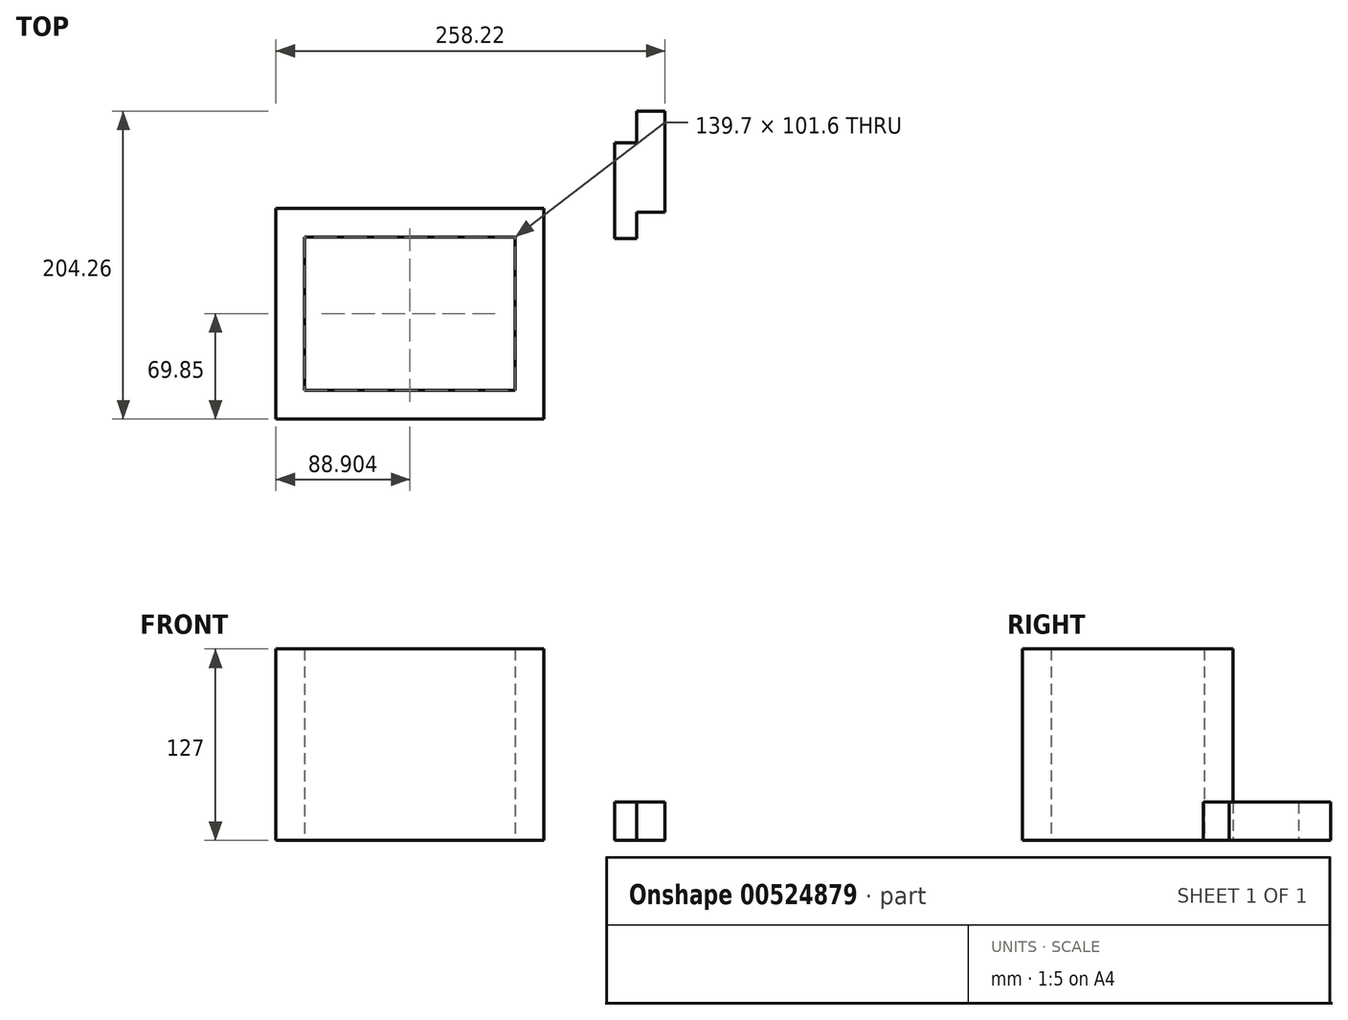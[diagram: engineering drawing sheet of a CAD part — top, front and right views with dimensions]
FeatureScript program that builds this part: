
annotation { "Feature Type Name" : "Feature", "Feature Type Description" : "" }
export const myFeature = defineFeature(function(context is Context, id is Id, definition is map)
    precondition{}
    {
        {
            var Q0;
            Q0=qCreatedBy(makeId("Top.planeOp"),FACE);
            var sketch = newSketch(context, id + "F0", { "sketchPlane" : qUnion([Q0])});
            skLineSegment(sketch, "E0.bottom", {"start": v(-316.12, 0) * mm, "end": v(-297.07, 0) * mm});
            skLineSegment(sketch, "E0.top", {"start": v(-316.12, -139.7) * mm, "end": v(-296.98, -139.7) * mm});
            skLineSegment(sketch, "E0.left", {"start": v(-316.12, 0) * mm, "end": v(-316.12, -139.7) * mm});
            skLineSegment(sketch, "E0.right", {"start": v(-138.32, 0) * mm, "end": v(-138.32, -139.7) * mm});
            skLineSegment(sketch, "E1", {"start": v(-157.37, 0) * mm, "end": v(-157.37, -139.7) * mm});
            skLineSegment(sketch, "E2", {"start": v(-297.07, 0) * mm, "end": v(-297.07, -139.7) * mm});
            skLineSegment(sketch, "E3", {"start": v(-297.07, -19.05) * mm, "end": v(-157.37, -19.05) * mm});
            skLineSegment(sketch, "E4", {"start": v(-297.07, -120.65) * mm, "end": v(-157.37, -120.65) * mm});
            skLineSegment(sketch, "E5", {"start": v(-297.07, 0) * mm, "end": v(-157.37, 0) * mm});
            skLineSegment(sketch, "E6", {"start": v(-157.37, 0) * mm, "end": v(-138.32, 0) * mm});
            skLineSegment(sketch, "E7", {"start": v(-157.37, -139.7) * mm, "end": v(-157.37, -139.7) * mm});
            skLineSegment(sketch, "E8", {"start": v(-296.98, -139.7) * mm, "end": v(-138.32, -139.7) * mm});
            skSolve(sketch);
        }
        {
            var Q0;
            Q0 = qSketchRegion(id + "F0", true);
            extrude(context, id + "F1", {"entities" : qUnion([Q0]), "depth" : 127 * mm, "offsetDistance" : 25.4 * mm});
        }
        {
            var Q0;
            Q0=qCreatedBy(makeId("Top.planeOp"),FACE);
            var sketch = newSketch(context, id + "F2", { "sketchPlane" : qUnion([Q0])});
            skLineSegment(sketch, "E9.bottom", {"start": v(-91.38, 43.53) * mm, "end": v(-76.79, 43.53) * mm});
            skLineSegment(sketch, "E9.top", {"start": v(-91.38, -19.88) * mm, "end": v(-76.79, -19.88) * mm});
            skLineSegment(sketch, "E9.left", {"start": v(-91.38, 43.53) * mm, "end": v(-91.38, -19.88) * mm});
            skLineSegment(sketch, "E9.right", {"start": v(-76.79, 43.53) * mm, "end": v(-76.79, -19.88) * mm});
            skLineSegment(sketch, "E10.bottom", {"start": v(-57.9, -2.56) * mm, "end": v(-76.79, -2.56) * mm});
            skLineSegment(sketch, "E10.top", {"start": v(-57.9, 64.56) * mm, "end": v(-76.79, 64.56) * mm});
            skLineSegment(sketch, "E10.left", {"start": v(-57.9, -2.56) * mm, "end": v(-57.9, 64.56) * mm});
            skLineSegment(sketch, "E10.right", {"start": v(-76.79, -2.56) * mm, "end": v(-76.79, 64.56) * mm});
            skSolve(sketch);
        }
        {
            var Q0;
            Q0 = qSketchRegion(id + "F2", true);
            extrude(context, id + "F3", {"entities" : qUnion([Q0]), "depth" : 25.4 * mm, "offsetDistance" : 25.4 * mm});
        }
    });
